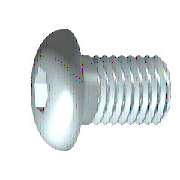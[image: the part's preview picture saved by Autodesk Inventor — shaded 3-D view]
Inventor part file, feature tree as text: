
AUTODESK INVENTOR PART (.ipt)
format: ipt  version: 2021.4 (Build 254397000, 397)  size: 205,824 bytes
history: native  units: mm (DEFAULTED — no unit token found)
features: sketch x2, extrude x1, plane x1, fillet x1
ambient origin geometry x7: Origin, YZ Plane, XY Plane, X Axis, Y Axis, Z Axis, Center Point
bodies: Solid1 (feature_tree), Body (feature_tree)
feature tree (5):
  extrude  "Slot"  Depth=3.3mm
  plane  "Work Plane1"
  fillet  "Fillet2"  Radius=3.3mm
  sketch  "Sketch1"  dims[d1=7.0mm d2=0.61355mm d3=3.3mm]
  sketch  "Sketch2"  dims[d4=2.08mm d5=60.0deg d6=6.0mm d7=6.0mm d8=4.618802mm d9=10.5mm d10=90.0deg d11=10.0mm d12=0.0mm d13=7.0mm d14=0.0mm d15=0.61345mm d16=0.61345mm d17=2.56mm d19=0.0mm d26=10.0mm d27=45.0deg d28=0.0mm d29=0.0mm d30=0.5mm]
